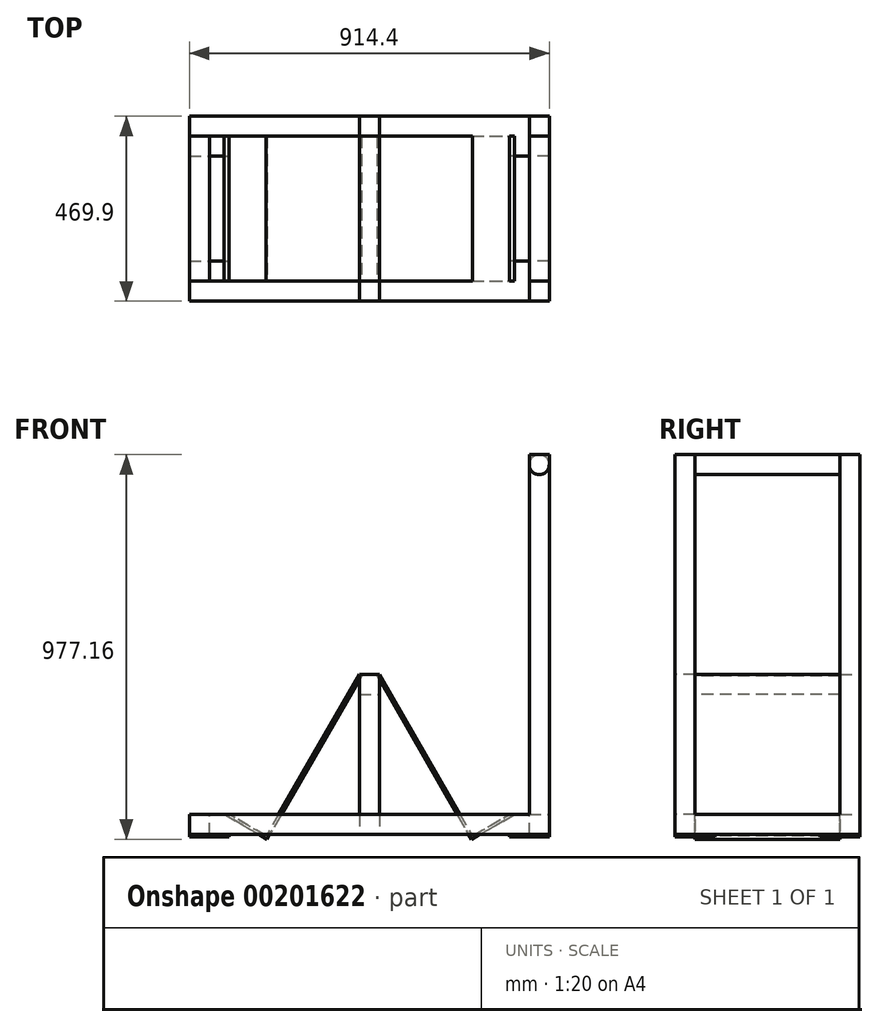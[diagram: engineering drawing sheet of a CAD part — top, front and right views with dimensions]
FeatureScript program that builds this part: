
annotation { "Feature Type Name" : "Feature", "Feature Type Description" : "" }
export const myFeature = defineFeature(function(context is Context, id is Id, definition is map)
    precondition{}
    {
        {
            var Q0;
            Q0=qCreatedBy(makeId("Front.planeOp"),FACE);
            var sketch = newSketch(context, id + "F0", { "sketchPlane" : qUnion([Q0])});
            skLineSegment(sketch, "E0.bottom", {"start": v(-457.2, 25.4) * mm, "end": v(457.2, 25.4) * mm});
            skLineSegment(sketch, "E0.top", {"start": v(-457.2, -25.4) * mm, "end": v(457.2, -25.4) * mm});
            skLineSegment(sketch, "E0.left", {"start": v(-457.2, 25.4) * mm, "end": v(-457.2, -25.4) * mm});
            skLineSegment(sketch, "E0.right", {"start": v(457.2, 25.4) * mm, "end": v(457.2, -25.4) * mm});
            skSolve(sketch);
        }
        {
            var Q0;
            Q0 = qSketchRegion(id + "F0", true);
            extrude(context, id + "F1", {"entities" : qUnion([Q0]), "depth" : 50.8 * mm});
        }
        {
            var Q0;
            Q0=makeQuery(id+"F1.opExtrude","CAP_FACE",FACE,{"disambiguationData":[OSD([sQuery(id+"F0.wireOp",EDGE,"E0.bottom"),sQuery(id+"F0.wireOp",EDGE,"E0.top"),sQuery(id+"F0.wireOp",EDGE,"E0.left"),sQuery(id+"F0.wireOp",EDGE,"E0.right")])],"isStart":false});
            var sketch = newSketch(context, id + "F2", { "sketchPlane" : qUnion([Q0])});
            skLineSegment(sketch, "E1.bottom", {"start": v(-25.4, 25.4) * mm, "end": v(25.4, 25.4) * mm});
            skLineSegment(sketch, "E1.top", {"start": v(-25.4, 381) * mm, "end": v(25.4, 381) * mm});
            skLineSegment(sketch, "E1.left", {"start": v(-25.4, 25.4) * mm, "end": v(-25.4, 381) * mm});
            skLineSegment(sketch, "E1.right", {"start": v(25.4, 25.4) * mm, "end": v(25.4, 381) * mm});
            skSolve(sketch);
        }
        {
            var Q0;
            Q0 = qSketchRegion(id + "F2", true);
            extrude(context, id + "F3", {"entities" : qUnion([Q0]), "oppositeDirection" : true, "depth" : 50.8 * mm});
        }
        {
            var Q0;
            Q0=makeQuery(id+"F3.opExtrude","CAP_FACE",FACE,{"disambiguationData":[OSD([sQuery(id+"F2.wireOp",EDGE,"E1.bottom"),sQuery(id+"F2.wireOp",EDGE,"E1.top"),sQuery(id+"F2.wireOp",EDGE,"E1.left"),sQuery(id+"F2.wireOp",EDGE,"E1.right")])],"isStart":false});
            var sketch = newSketch(context, id + "F4", { "sketchPlane" : qUnion([Q0])});
            skLineSegment(sketch, "E2", {"start": v(25.4, 381) * mm, "end": v(261.93, -28.68) * mm});
            skLineSegment(sketch, "E3", {"start": v(261.93, -28.68) * mm, "end": v(355.6, 25.4) * mm});
            skLineSegment(sketch, "E4", {"start": v(25.4, 381) * mm, "end": v(19.9, 377.83) * mm});
            skLineSegment(sketch, "E5", {"start": v(19.9, 377.83) * mm, "end": v(259.6, -37.36) * mm});
            skLineSegment(sketch, "E6", {"start": v(259.6, -37.36) * mm, "end": v(368.3, 25.4) * mm});
            skLineSegment(sketch, "E7", {"start": v(368.3, 25.4) * mm, "end": v(355.6, 25.4) * mm});
            skSolve(sketch);
        }
        {
            var Q0;
            Q0 = qSketchRegion(id + "F4", true);
            extrude(context, id + "F5", {"entities" : qUnion([Q0]), "depth" : 368.3 * mm});
        }
        {
            var Q0;
            Q0=makeQuery(id+"F1.opExtrude","SWEPT_FACE",FACE,{"disambiguationData":[OSD([sQuery(id+"F0.wireOp",EDGE,"E0.bottom")])]});
            var sketch = newSketch(context, id + "F6", { "sketchPlane" : qUnion([Q0])});
            skLineSegment(sketch, "E8.bottom", {"start": v(-457.2, 0) * mm, "end": v(-406.4, 0) * mm});
            skLineSegment(sketch, "E8.top", {"start": v(-457.2, 368.3) * mm, "end": v(-406.4, 368.3) * mm});
            skLineSegment(sketch, "E8.left", {"start": v(-457.2, 0) * mm, "end": v(-457.2, 368.3) * mm});
            skLineSegment(sketch, "E8.right", {"start": v(-406.4, 0) * mm, "end": v(-406.4, 368.3) * mm});
            skSolve(sketch);
        }
        {
            var Q0;
            Q0 = qSketchRegion(id + "F6", true);
            extrude(context, id + "F7", {"entities" : qUnion([Q0]), "oppositeDirection" : true, "depth" : 50.8 * mm});
        }
        {
            var Q0;
            Q0=makeQuery(id+"F7.opExtrude","SWEPT_FACE",FACE,{"disambiguationData":[OSD([sQuery(id+"F6.wireOp",EDGE,"E8.left")])]});
            var sketch = newSketch(context, id + "F8", { "sketchPlane" : qUnion([Q0])});
            skLineSegment(sketch, "E9.bottom", {"start": v(-368.3, -25.4) * mm, "end": v(-419.1, -25.4) * mm});
            skLineSegment(sketch, "E9.top", {"start": v(-368.3, 25.4) * mm, "end": v(-419.1, 25.4) * mm});
            skLineSegment(sketch, "E9.left", {"start": v(-368.3, -25.4) * mm, "end": v(-368.3, 25.4) * mm});
            skLineSegment(sketch, "E9.right", {"start": v(-419.1, -25.4) * mm, "end": v(-419.1, 25.4) * mm});
            skSolve(sketch);
        }
        {
            var Q0;
            Q0 = qSketchRegion(id + "F8", true);
            extrude(context, id + "F9", {"entities" : qUnion([Q0]), "oppositeDirection" : true, "depth" : 914.4 * mm});
        }
        {
            var Q0;
            Q0=makeQuery(id+"F1.opExtrude","CAP_FACE",FACE,{"disambiguationData":[OSD([sQuery(id+"F0.wireOp",EDGE,"E0.bottom"),sQuery(id+"F0.wireOp",EDGE,"E0.top"),sQuery(id+"F0.wireOp",EDGE,"E0.left"),sQuery(id+"F0.wireOp",EDGE,"E0.right")])],"isStart":true});
            var sketch = newSketch(context, id + "F10", { "sketchPlane" : qUnion([Q0])});
            skLineSegment(sketch, "E10.bottom", {"start": v(25.4, 25.4) * mm, "end": v(-25.4, 25.4) * mm});
            skLineSegment(sketch, "E10.top", {"start": v(25.4, -25.4) * mm, "end": v(-25.4, -25.4) * mm});
            skLineSegment(sketch, "E10.left", {"start": v(25.4, 25.4) * mm, "end": v(25.4, -25.4) * mm});
            skLineSegment(sketch, "E10.right", {"start": v(-25.4, 25.4) * mm, "end": v(-25.4, -25.4) * mm});
            skSolve(sketch);
        }
        {
            var Q0;
            Q0 = qSketchRegion(id + "F10", true);
            extrude(context, id + "F11", {"entities" : qUnion([Q0]), "depth" : 368.3 * mm});
        }
        {
            var Q0;
            Q0=makeQuery(id+"F3.opExtrude","CAP_FACE",FACE,{"disambiguationData":[OSD([sQuery(id+"F2.wireOp",EDGE,"E1.bottom"),sQuery(id+"F2.wireOp",EDGE,"E1.top"),sQuery(id+"F2.wireOp",EDGE,"E1.left"),sQuery(id+"F2.wireOp",EDGE,"E1.right")])],"isStart":false});
            var sketch = newSketch(context, id + "F12", { "sketchPlane" : qUnion([Q0])});
            skLineSegment(sketch, "E11.bottom", {"start": v(25.4, 381) * mm, "end": v(-25.4, 381) * mm});
            skLineSegment(sketch, "E11.top", {"start": v(25.4, 330.2) * mm, "end": v(-25.4, 330.2) * mm});
            skLineSegment(sketch, "E11.left", {"start": v(25.4, 381) * mm, "end": v(25.4, 330.2) * mm});
            skLineSegment(sketch, "E11.right", {"start": v(-25.4, 381) * mm, "end": v(-25.4, 330.2) * mm});
            skSolve(sketch);
        }
        {
            var Q0;
            Q0 = qSketchRegion(id + "F12", true);
            extrude(context, id + "F13", {"entities" : qUnion([Q0]), "depth" : 368.3 * mm});
        }
        {
            var Q0;
            Q0=makeQuery(id+"F11.opExtrude","SWEPT_FACE",FACE,{"disambiguationData":[OSD([sQuery(id+"F10.wireOp",EDGE,"E10.bottom")])]});
            var sketch = newSketch(context, id + "F14", { "sketchPlane" : qUnion([Q0])});
            skLineSegment(sketch, "E12.bottom", {"start": v(-25.4, 368.3) * mm, "end": v(25.4, 368.3) * mm});
            skLineSegment(sketch, "E12.top", {"start": v(-25.4, 419.1) * mm, "end": v(25.4, 419.1) * mm});
            skLineSegment(sketch, "E12.left", {"start": v(-25.4, 368.3) * mm, "end": v(-25.4, 419.1) * mm});
            skLineSegment(sketch, "E12.right", {"start": v(25.4, 368.3) * mm, "end": v(25.4, 419.1) * mm});
            skSolve(sketch);
        }
        {
            var Q0;
            Q0 = qSketchRegion(id + "F14", true);
            extrude(context, id + "F15", {"entities" : qUnion([Q0]), "depth" : 355.6 * mm});
        }
        {
            var Q0;
            Q0=makeQuery(id+"F5.opExtrude","SWEPT_BODY",BODY,{"disambiguationData":[OSD([sQuery(id+"F4.wireOp",EDGE,"E2"),sQuery(id+"F4.wireOp",EDGE,"E3"),sQuery(id+"F4.wireOp",EDGE,"E4"),sQuery(id+"F4.wireOp",EDGE,"E5"),sQuery(id+"F4.wireOp",EDGE,"E6"),sQuery(id+"F4.wireOp",EDGE,"E7")])]});
            var Q1;
            Q1=makeQuery(id+"F7.opExtrude","SWEPT_BODY",BODY,{"disambiguationData":[OSD([sQuery(id+"F6.wireOp",EDGE,"E8.bottom"),sQuery(id+"F6.wireOp",EDGE,"E8.top"),sQuery(id+"F6.wireOp",EDGE,"E8.left"),sQuery(id+"F6.wireOp",EDGE,"E8.right")])]});
            var Q2;
            Q2=qCreatedBy(makeId("Right.planeOp"),FACE);
            mirror(context, id + "F16", {"entities" : qUnion([Q0, Q1]), "mirrorPlane" : qUnion([Q2])});
        }
        {
            var Q0;
            Q0=makeQuery(id+"F1.opExtrude","SWEPT_FACE",FACE,{"disambiguationData":[OSD([sQuery(id+"F0.wireOp",EDGE,"E0.bottom")])]});
            var sketch = newSketch(context, id + "F17", { "sketchPlane" : qUnion([Q0])});
            skLineSegment(sketch, "E13.bottom", {"start": v(457.2, -50.8) * mm, "end": v(406.4, -50.8) * mm});
            skLineSegment(sketch, "E13.top", {"start": v(457.2, 0) * mm, "end": v(406.4, 0) * mm});
            skLineSegment(sketch, "E13.left", {"start": v(457.2, -50.8) * mm, "end": v(457.2, 0) * mm});
            skLineSegment(sketch, "E13.right", {"start": v(406.4, -50.8) * mm, "end": v(406.4, 0) * mm});
            skSolve(sketch);
        }
        {
            var Q0;
            Q0 = qSketchRegion(id + "F17", true);
            extrude(context, id + "F18", {"entities" : qUnion([Q0]), "operationType" : NewBodyOperationType.ADD, "depth" : 914.4 * mm});
        }
        {
            var Q0;
            Q0=makeQuery(id+"F9.opExtrude","SWEPT_FACE",FACE,{"disambiguationData":[OSD([sQuery(id+"F8.wireOp",EDGE,"E9.top")])]});
            var sketch = newSketch(context, id + "F19", { "sketchPlane" : qUnion([Q0])});
            skLineSegment(sketch, "E14.bottom", {"start": v(457.2, 368.3) * mm, "end": v(406.4, 368.3) * mm});
            skLineSegment(sketch, "E14.top", {"start": v(457.2, 419.1) * mm, "end": v(406.4, 419.1) * mm});
            skLineSegment(sketch, "E14.left", {"start": v(457.2, 368.3) * mm, "end": v(457.2, 419.1) * mm});
            skLineSegment(sketch, "E14.right", {"start": v(406.4, 368.3) * mm, "end": v(406.4, 419.1) * mm});
            skSolve(sketch);
        }
        {
            var Q0;
            Q0 = qSketchRegion(id + "F19", true);
            extrude(context, id + "F20", {"entities" : qUnion([Q0]), "operationType" : NewBodyOperationType.ADD, "depth" : 914.4 * mm});
        }
        {
            var Q0;
            Q0=makeQuery(id+"F20.boolean.opBoolean","MERGE",FACE,{"derivedFrom":[makeQuery(id+"F9.opExtrude","SWEPT_FACE",FACE,{"disambiguationData":[OSD([sQuery(id+"F8.wireOp",EDGE,"E9.left")])]}),makeQuery(id+"F20.opExtrude","SWEPT_FACE",FACE,{"disambiguationData":[OSD([sQuery(id+"F19.wireOp",EDGE,"E14.bottom")])]})]});
            var sketch = newSketch(context, id + "F21", { "sketchPlane" : qUnion([Q0])});
            skCircle(sketch, "E15", {"center": v(431.8, 914.4) * mm, "radius": 25.4 * mm});
            skPoint(sketch, "E15.centerSnap0", {"position": v(431.8, 939.8) * mm});
            skSolve(sketch);
        }
        {
            var Q0;
            Q0 = qSketchRegion(id + "F21", true);
            extrude(context, id + "F22", {"entities" : qUnion([Q0]), "depth" : 368.3 * mm});
        }
        {
            var Q0;
            Q0=makeQuery(id+"F1.opExtrude","SWEPT_FACE",FACE,{"disambiguationData":[OSD([sQuery(id+"F0.wireOp",EDGE,"E0.top")])]});
            var sketch = newSketch(context, id + "F23", { "sketchPlane" : qUnion([Q0])});
            skLineSegment(sketch, "E16.bottom", {"start": v(-457.2, 50.8) * mm, "end": v(-355.6, 50.8) * mm});
            skLineSegment(sketch, "E16.top", {"start": v(-457.2, -50.8) * mm, "end": v(-355.6, -50.8) * mm});
            skLineSegment(sketch, "E16.left", {"start": v(-457.2, 50.8) * mm, "end": v(-457.2, -50.8) * mm});
            skLineSegment(sketch, "E16.right", {"start": v(-355.6, 50.8) * mm, "end": v(-355.6, -50.8) * mm});
            skLineSegment(sketch, "E17.bottom", {"start": v(457.2, 50.8) * mm, "end": v(355.6, 50.8) * mm});
            skLineSegment(sketch, "E17.top", {"start": v(457.2, -50.8) * mm, "end": v(355.6, -50.8) * mm});
            skLineSegment(sketch, "E17.left", {"start": v(457.2, 50.8) * mm, "end": v(457.2, -50.8) * mm});
            skLineSegment(sketch, "E17.right", {"start": v(355.6, 50.8) * mm, "end": v(355.6, -50.8) * mm});
            skSolve(sketch);
        }
        {
            var Q0;
            Q0 = qSketchRegion(id + "F23", true);
            extrude(context, id + "F24", {"entities" : qUnion([Q0]), "depth" : 6.35 * mm});
        }
        {
            var Q0;
            Q0=makeQuery(id+"F9.opExtrude","SWEPT_FACE",FACE,{"disambiguationData":[OSD([sQuery(id+"F8.wireOp",EDGE,"E9.bottom")])]});
            var sketch = newSketch(context, id + "F25", { "sketchPlane" : qUnion([Q0])});
            skLineSegment(sketch, "E18.bottom", {"start": v(-457.2, -419.1) * mm, "end": v(-355.6, -419.1) * mm});
            skLineSegment(sketch, "E18.top", {"start": v(-457.2, -317.5) * mm, "end": v(-355.6, -317.5) * mm});
            skLineSegment(sketch, "E18.left", {"start": v(-457.2, -419.1) * mm, "end": v(-457.2, -317.5) * mm});
            skLineSegment(sketch, "E18.right", {"start": v(-355.6, -419.1) * mm, "end": v(-355.6, -317.5) * mm});
            skLineSegment(sketch, "E19.bottom", {"start": v(457.2, -419.1) * mm, "end": v(355.6, -419.1) * mm});
            skLineSegment(sketch, "E19.top", {"start": v(457.2, -317.5) * mm, "end": v(355.6, -317.5) * mm});
            skLineSegment(sketch, "E19.left", {"start": v(457.2, -419.1) * mm, "end": v(457.2, -317.5) * mm});
            skLineSegment(sketch, "E19.right", {"start": v(355.6, -419.1) * mm, "end": v(355.6, -317.5) * mm});
            skSolve(sketch);
        }
        {
            var Q0;
            Q0 = qSketchRegion(id + "F25", true);
            extrude(context, id + "F26", {"entities" : qUnion([Q0]), "depth" : 6.35 * mm});
        }
    });
